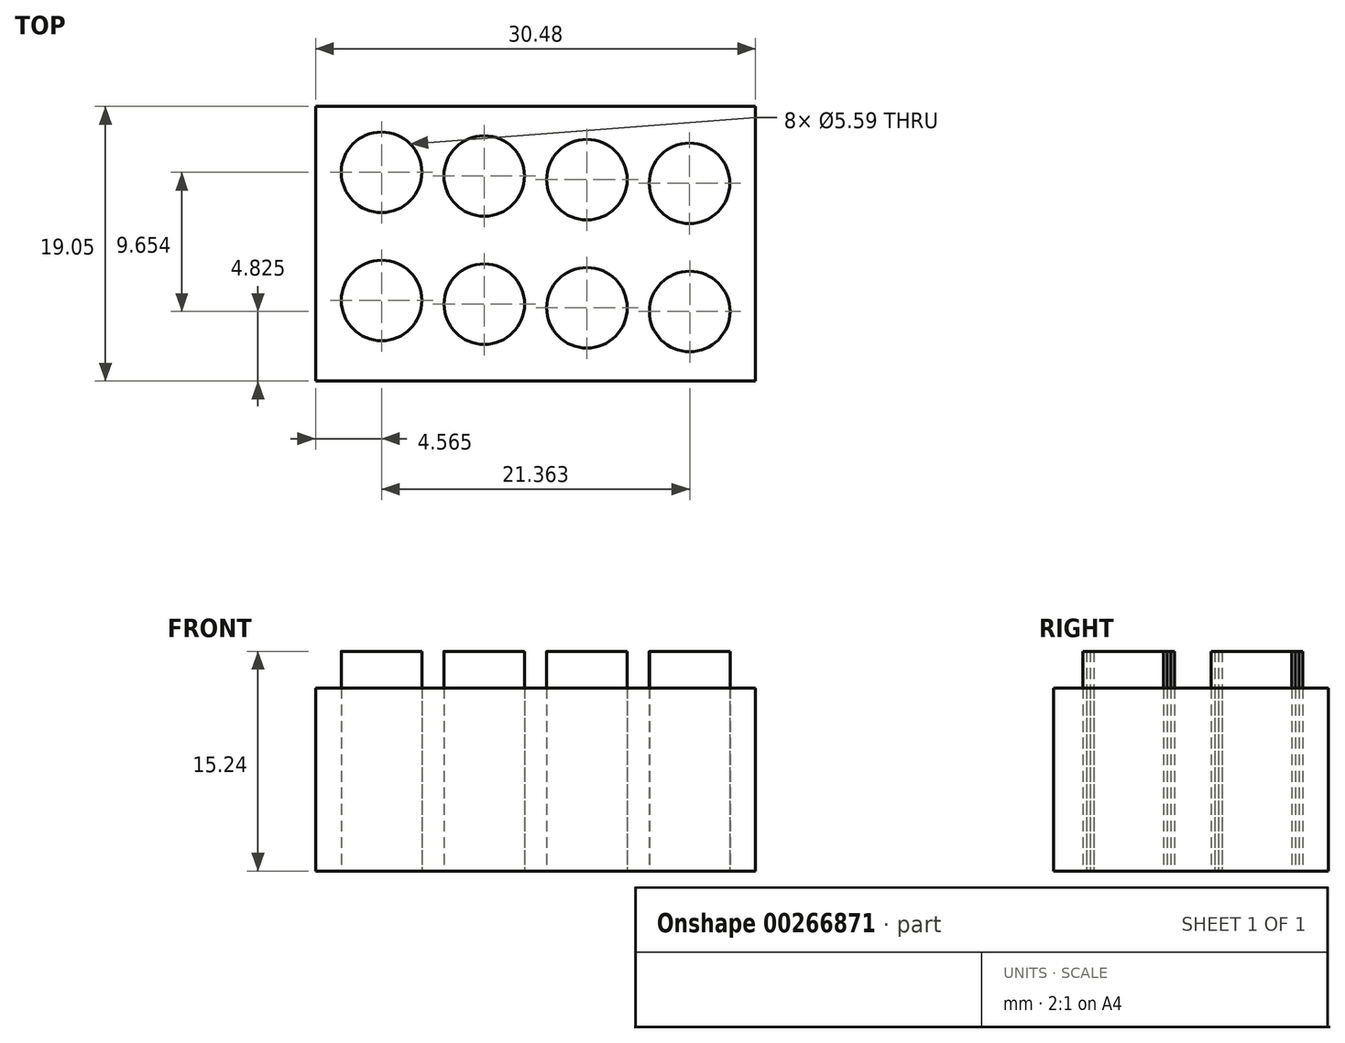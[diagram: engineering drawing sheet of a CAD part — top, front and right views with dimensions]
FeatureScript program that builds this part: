
annotation { "Feature Type Name" : "Feature", "Feature Type Description" : "" }
export const myFeature = defineFeature(function(context is Context, id is Id, definition is map)
    precondition{}
    {
        {
            var Q0;
            Q0=qCreatedBy(makeId("Top.planeOp"),FACE);
            var sketch = newSketch(context, id + "F0", { "sketchPlane" : qUnion([Q0])});
            skLineSegment(sketch, "E0.bottom", {"start": v(0, 19.05) * mm, "end": v(30.48, 19.05) * mm});
            skLineSegment(sketch, "E0.top", {"start": v(0, 0) * mm, "end": v(30.48, 0) * mm});
            skLineSegment(sketch, "E0.left", {"start": v(0, 19.05) * mm, "end": v(0, 0) * mm});
            skLineSegment(sketch, "E0.right", {"start": v(30.48, 19.05) * mm, "end": v(30.48, 0) * mm});
            skCircle(sketch, "E1", {"center": v(4.57, 14.48) * mm, "radius": 2.8 * mm});
            skCircle(sketch, "E2.0.1.0", {"center": v(4.57, 5.59) * mm, "radius": 2.8 * mm});
            skCircle(sketch, "E2.1.0.0", {"center": v(11.68, 14.22) * mm, "radius": 2.8 * mm});
            skCircle(sketch, "E2.1.1.0", {"center": v(11.7, 5.33) * mm, "radius": 2.8 * mm});
            skCircle(sketch, "E2.2.0.0", {"center": v(18.8, 13.97) * mm, "radius": 2.8 * mm});
            skCircle(sketch, "E2.2.1.0", {"center": v(18.8, 5.08) * mm, "radius": 2.8 * mm});
            skCircle(sketch, "E2.3.0.0", {"center": v(25.92, 13.72) * mm, "radius": 2.8 * mm});
            skCircle(sketch, "E2.3.1.0", {"center": v(25.93, 4.82) * mm, "radius": 2.8 * mm});
            skLineSegment(sketch, "E2.direction1", {"start": v(4.57, 14.48) * mm, "end": v(11.68, 14.22) * mm, "construction": true});
            skLineSegment(sketch, "E2.direction2", {"start": v(4.57, 14.48) * mm, "end": v(4.57, 5.59) * mm, "construction": true});
            skSolve(sketch);
        }
        {
            var Q0;
            Q0=makeQuery(id+"F0.imprint","IMPRINT",FACE,{"disambiguationData":[TD([[makeQuery(id+"F0.imprint","IMPRINT",EDGE,{"derivedFrom":sQuery(id+"F0.wireOp",EDGE,"E1")}),1.0]])]});
            var Q1;
            Q1=makeQuery(id+"F0.imprint","IMPRINT",FACE,{"disambiguationData":[TD([[makeQuery(id+"F0.imprint","IMPRINT",EDGE,{"derivedFrom":sQuery(id+"F0.wireOp",EDGE,"E2.1.0.0")}),1.0]])]});
            var Q2;
            Q2=makeQuery(id+"F0.imprint","IMPRINT",FACE,{"disambiguationData":[TD([[makeQuery(id+"F0.imprint","IMPRINT",EDGE,{"derivedFrom":sQuery(id+"F0.wireOp",EDGE,"E2.2.0.0")}),1.0]])]});
            var Q3;
            Q3=makeQuery(id+"F0.imprint","IMPRINT",FACE,{"disambiguationData":[TD([[makeQuery(id+"F0.imprint","IMPRINT",EDGE,{"derivedFrom":sQuery(id+"F0.wireOp",EDGE,"E2.3.0.0")}),1.0]])]});
            var Q4;
            Q4=makeQuery(id+"F0.imprint","IMPRINT",FACE,{"disambiguationData":[TD([[makeQuery(id+"F0.imprint","IMPRINT",EDGE,{"derivedFrom":sQuery(id+"F0.wireOp",EDGE,"E2.3.1.0")}),1.0]])]});
            var Q5;
            Q5=makeQuery(id+"F0.imprint","IMPRINT",FACE,{"disambiguationData":[TD([[makeQuery(id+"F0.imprint","IMPRINT",EDGE,{"derivedFrom":sQuery(id+"F0.wireOp",EDGE,"E2.2.1.0")}),1.0]])]});
            var Q6;
            Q6=makeQuery(id+"F0.imprint","IMPRINT",FACE,{"disambiguationData":[TD([[makeQuery(id+"F0.imprint","IMPRINT",EDGE,{"derivedFrom":sQuery(id+"F0.wireOp",EDGE,"E2.1.1.0")}),1.0]])]});
            var Q7;
            Q7=makeQuery(id+"F0.imprint","IMPRINT",FACE,{"disambiguationData":[TD([[makeQuery(id+"F0.imprint","IMPRINT",EDGE,{"derivedFrom":sQuery(id+"F0.wireOp",EDGE,"E2.0.1.0")}),1.0]])]});
            extrude(context, id + "F1", {"entities" : qUnion([Q0, Q1, Q2, Q3, Q4, Q5, Q6, Q7]), "depth" : 15.24 * mm});
        }
        {
            var Q0;
            Q0 = qSketchRegion(id + "F0", true);
            extrude(context, id + "F2", {"entities" : qUnion([Q0]), "depth" : 12.7 * mm});
        }
    });
